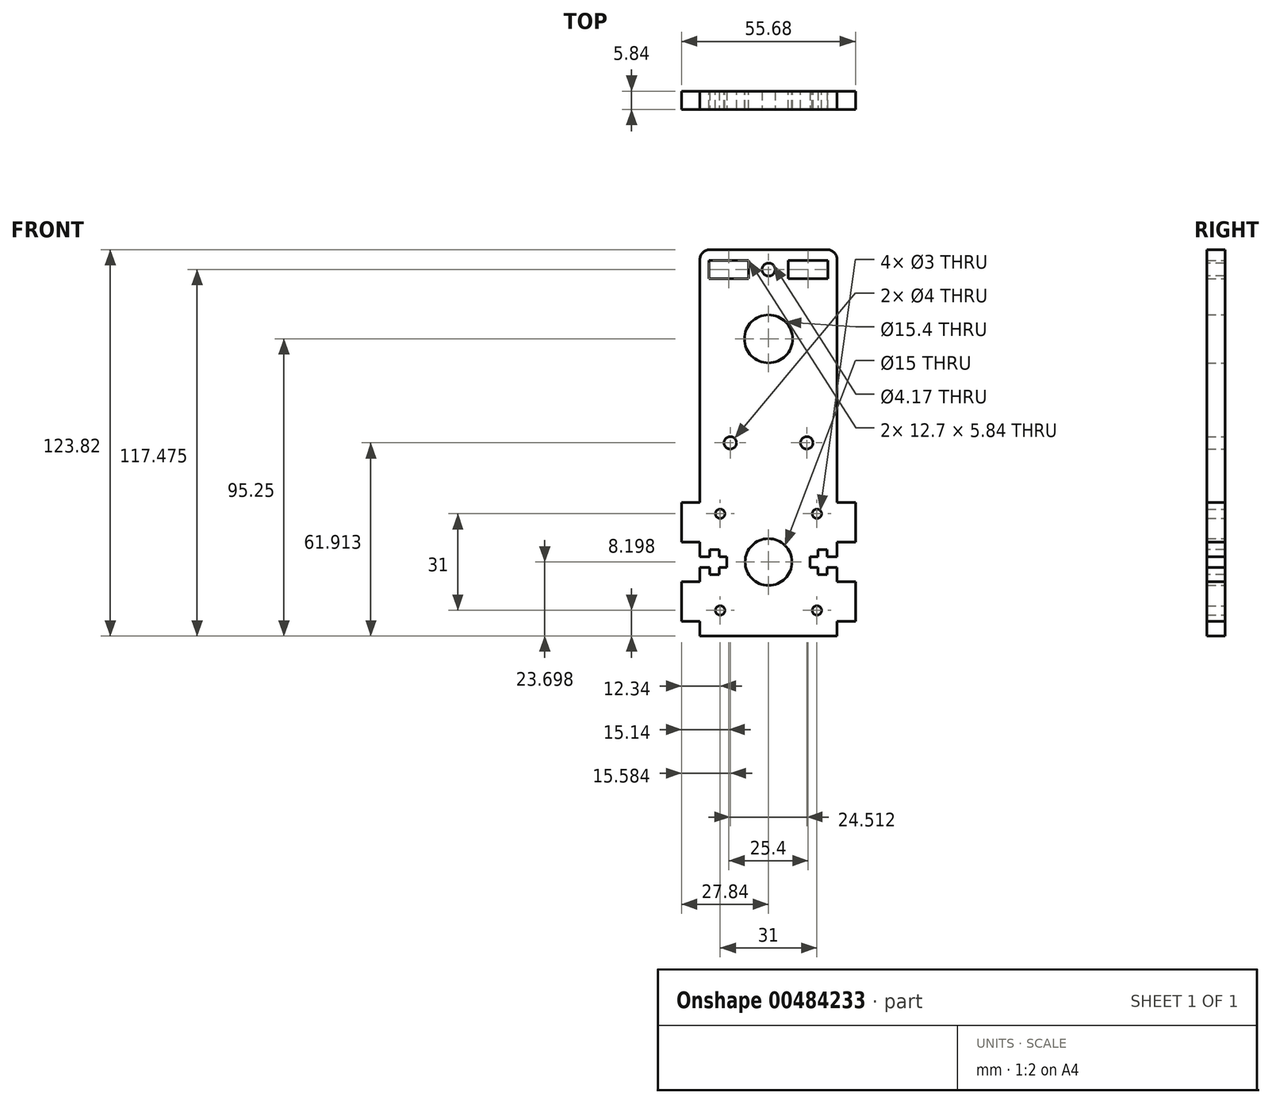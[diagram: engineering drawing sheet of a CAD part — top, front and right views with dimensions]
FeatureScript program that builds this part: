
annotation { "Feature Type Name" : "Feature", "Feature Type Description" : "" }
export const myFeature = defineFeature(function(context is Context, id is Id, definition is map)
    precondition{}
    {
        {
            var Q0;
            Q0=qCreatedBy(makeId("Front.planeOp"),FACE);
            var sketch = newSketch(context, id + "F0", { "sketchPlane" : qUnion([Q0])});
            skCircle(sketch, "E0", {"center": v(0, 0) * mm, "radius": 7.7 * mm});
            skCircle(sketch, "E1", {"center": v(0, 0) * mm, "radius": 8 * mm, "construction": true});
            skCircle(sketch, "E2", {"center": v(0, -71.55) * mm, "radius": 7.5 * mm});
            skLineSegment(sketch, "E3.bottom", {"start": v(-22, 28.58) * mm, "end": v(22, 28.58) * mm});
            skLineSegment(sketch, "E3.top", {"start": v(-22, -95.25) * mm, "end": v(22, -95.25) * mm});
            skLineSegment(sketch, "E3.right", {"start": v(22, 28.58) * mm, "end": v(22, -52.5) * mm});
            skPoint(sketch, "E3.middle", {"position": v(0, -33.34) * mm});
            skCircle(sketch, "E4", {"center": v(0, 0) * mm, "radius": 15.88 * mm, "construction": true});
            skLineSegment(sketch, "E5.bottom", {"start": v(-21.15, -50.4) * mm, "end": v(21.15, -50.4) * mm, "construction": true});
            skLineSegment(sketch, "E5.top", {"start": v(-21.15, -92.7) * mm, "end": v(21.15, -92.7) * mm, "construction": true});
            skLineSegment(sketch, "E5.left", {"start": v(-21.15, -50.4) * mm, "end": v(-21.15, -92.7) * mm, "construction": true});
            skLineSegment(sketch, "E5.right", {"start": v(21.15, -50.4) * mm, "end": v(21.15, -92.7) * mm, "construction": true});
            skLineSegment(sketch, "E6", {"start": v(-15.77, -1.86) * mm, "end": v(-7.45, -72.43) * mm, "construction": true});
            skLineSegment(sketch, "E7", {"start": v(0, 0) * mm, "end": v(0, -71.55) * mm, "construction": true});
            skLineSegment(sketch, "E8.MirrorCS", {"start": v(15.77, -1.86) * mm, "end": v(7.45, -72.43) * mm, "construction": true});
            skLineSegment(sketch, "E9", {"start": v(-21.15, -71.55) * mm, "end": v(21.15, -71.55) * mm, "construction": true});
            skLineSegment(sketch, "E10", {"start": v(0, -92.7) * mm, "end": v(0, -50.4) * mm, "construction": true});
            skCircle(sketch, "E11", {"center": v(-15.5, -56.05) * mm, "radius": 1.5 * mm});
            skCircle(sketch, "E12.MirrorC", {"center": v(15.5, -56.05) * mm, "radius": 1.5 * mm});
            skCircle(sketch, "E13.MirrorC", {"center": v(15.5, -87.05) * mm, "radius": 1.5 * mm});
            skCircle(sketch, "E14.MirrorC", {"center": v(-15.5, -87.05) * mm, "radius": 1.5 * mm});
            skLineSegment(sketch, "E15.bottom", {"start": v(-22, -77.9) * mm, "end": v(-27.84, -77.9) * mm});
            skLineSegment(sketch, "E15.top", {"start": v(-22, -90.6) * mm, "end": v(-27.84, -90.6) * mm});
            skLineSegment(sketch, "E15.right", {"start": v(-27.84, -77.9) * mm, "end": v(-27.84, -90.6) * mm});
            skPoint(sketch, "E15.middle", {"position": v(-24.92, -84.25) * mm});
            skLineSegment(sketch, "E16.MirrorCS", {"start": v(-22, -65.2) * mm, "end": v(-27.84, -65.2) * mm});
            skLineSegment(sketch, "E17.MirrorCS", {"start": v(-27.84, -65.2) * mm, "end": v(-27.84, -52.5) * mm});
            skLineSegment(sketch, "E18.MirrorCS", {"start": v(-22, -52.5) * mm, "end": v(-27.84, -52.5) * mm});
            skLineSegment(sketch, "E19.trimOffspring", {"start": v(-22, -65.2) * mm, "end": v(-22, -77.9) * mm});
            skLineSegment(sketch, "E20.trimOffspring", {"start": v(-22, -90.6) * mm, "end": v(-22, -95.25) * mm});
            skLineSegment(sketch, "E21", {"start": v(-22, -52.5) * mm, "end": v(-22, 28.58) * mm});
            skLineSegment(sketch, "E22.bottom", {"start": v(-6.35, 25.15) * mm, "end": v(-19.05, 25.15) * mm});
            skLineSegment(sketch, "E22.top", {"start": v(-6.35, 19.3) * mm, "end": v(-19.05, 19.3) * mm});
            skLineSegment(sketch, "E22.left", {"start": v(-6.35, 25.15) * mm, "end": v(-6.35, 19.3) * mm});
            skLineSegment(sketch, "E22.right", {"start": v(-19.05, 25.15) * mm, "end": v(-19.05, 19.3) * mm});
            skPoint(sketch, "E22.middle", {"position": v(-12.7, 22.23) * mm});
            skLineSegment(sketch, "E23.MirrorCS", {"start": v(6.35, 25.15) * mm, "end": v(6.35, 19.3) * mm});
            skLineSegment(sketch, "E24.MirrorCS", {"start": v(6.35, 25.15) * mm, "end": v(19.05, 25.15) * mm});
            skLineSegment(sketch, "E25.MirrorCS", {"start": v(19.05, 25.15) * mm, "end": v(19.05, 19.3) * mm});
            skLineSegment(sketch, "E26.MirrorCS", {"start": v(6.35, 19.3) * mm, "end": v(19.05, 19.3) * mm});
            skLineSegment(sketch, "E27.MirrorCS", {"start": v(22, -52.5) * mm, "end": v(27.84, -52.5) * mm});
            skLineSegment(sketch, "E28.MirrorCS", {"start": v(27.84, -65.2) * mm, "end": v(27.84, -52.5) * mm});
            skLineSegment(sketch, "E29.MirrorCS", {"start": v(22, -77.9) * mm, "end": v(27.84, -77.9) * mm});
            skLineSegment(sketch, "E30.MirrorCS", {"start": v(27.84, -77.9) * mm, "end": v(27.84, -90.6) * mm});
            skLineSegment(sketch, "E31.MirrorCS", {"start": v(22, -90.6) * mm, "end": v(27.84, -90.6) * mm});
            skLineSegment(sketch, "E32", {"start": v(27.84, -65.2) * mm, "end": v(22, -65.2) * mm});
            skLineSegment(sketch, "E33.trimOffspring", {"start": v(22, -65.2) * mm, "end": v(22, -77.9) * mm});
            skLineSegment(sketch, "E34.trimOffspring", {"start": v(22, -90.6) * mm, "end": v(22, -95.25) * mm});
            skLineSegment(sketch, "E35", {"start": v(0, -33.34) * mm, "end": v(22, -33.34) * mm, "construction": true});
            skLineSegment(sketch, "E36", {"start": v(0, -33.34) * mm, "end": v(-22, -33.34) * mm, "construction": true});
            skCircle(sketch, "E37", {"center": v(-12.26, -33.34) * mm, "radius": 2 * mm});
            skPoint(sketch, "E38", {"position": v(-12.06, -33.34) * mm});
            skCircle(sketch, "E39.MirrorC", {"center": v(12.26, -33.34) * mm, "radius": 2 * mm});
            skSolve(sketch);
        }
        {
            var Q0;
            Q0=qSketchRegion(id+"F0",true);
            extrude(context, id + "F1", {"entities" : qUnion([Q0]), "depth" : 5.84 * mm});
        }
        {
            var Q0;
            Q0=makeQuery(id+"F1.opExtrude","SWEPT_EDGE",EDGE,{"disambiguationData":[OSD([sQuery(id+"F0.wireOp",EDGE,"E3.bottom"),sQuery(id+"F0.wireOp",EDGE,"E21")])]});
            var Q1;
            Q1=makeQuery(id+"F1.opExtrude","SWEPT_EDGE",EDGE,{"disambiguationData":[OSD([sQuery(id+"F0.wireOp",EDGE,"E3.bottom"),sQuery(id+"F0.wireOp",EDGE,"E3.right")])]});
            fillet(context, id + "F2", {"entities" : qUnion([Q0, Q1]), "radius" : 3.17 * mm, "tangentPropagation" : true, "allowEdgeOverflow" : false});
        }
        {
            var Q0;
            Q0=makeQuery(id+"F1.opExtrude","CAP_FACE",FACE,{"disambiguationData":[OSD([sQuery(id+"F0.wireOp",EDGE,"E0"),sQuery(id+"F0.wireOp",EDGE,"E2"),sQuery(id+"F0.wireOp",EDGE,"E3.bottom"),sQuery(id+"F0.wireOp",EDGE,"E3.top"),sQuery(id+"F0.wireOp",EDGE,"E3.right"),sQuery(id+"F0.wireOp",EDGE,"E12.MirrorC"),sQuery(id+"F0.wireOp",EDGE,"E11"),sQuery(id+"F0.wireOp",EDGE,"E13.MirrorC"),sQuery(id+"F0.wireOp",EDGE,"E14.MirrorC"),sQuery(id+"F0.wireOp",EDGE,"E15.bottom"),sQuery(id+"F0.wireOp",EDGE,"E15.top"),sQuery(id+"F0.wireOp",EDGE,"E15.right"),sQuery(id+"F0.wireOp",EDGE,"E16.MirrorCS"),sQuery(id+"F0.wireOp",EDGE,"E17.MirrorCS"),sQuery(id+"F0.wireOp",EDGE,"E18.MirrorCS"),sQuery(id+"F0.wireOp",EDGE,"E19.trimOffspring"),sQuery(id+"F0.wireOp",EDGE,"E20.trimOffspring"),sQuery(id+"F0.wireOp",EDGE,"E21"),sQuery(id+"F0.wireOp",EDGE,"E22.bottom"),sQuery(id+"F0.wireOp",EDGE,"E22.top"),sQuery(id+"F0.wireOp",EDGE,"E22.left"),sQuery(id+"F0.wireOp",EDGE,"E22.right"),sQuery(id+"F0.wireOp",EDGE,"E23.MirrorCS"),sQuery(id+"F0.wireOp",EDGE,"E24.MirrorCS"),sQuery(id+"F0.wireOp",EDGE,"E25.MirrorCS"),sQuery(id+"F0.wireOp",EDGE,"E26.MirrorCS"),sQuery(id+"F0.wireOp",EDGE,"E27.MirrorCS"),sQuery(id+"F0.wireOp",EDGE,"E28.MirrorCS"),sQuery(id+"F0.wireOp",EDGE,"E29.MirrorCS"),sQuery(id+"F0.wireOp",EDGE,"E30.MirrorCS"),sQuery(id+"F0.wireOp",EDGE,"E31.MirrorCS"),sQuery(id+"F0.wireOp",EDGE,"E32"),sQuery(id+"F0.wireOp",EDGE,"E33.trimOffspring"),sQuery(id+"F0.wireOp",EDGE,"E34.trimOffspring"),sQuery(id+"F0.wireOp",EDGE,"E37"),sQuery(id+"F0.wireOp",EDGE,"E39.MirrorC")])],"isStart":false});
            var sketch = newSketch(context, id + "F3", { "sketchPlane" : qUnion([Q0])});
            skLineSegment(sketch, "E40", {"start": v(-22, -71.55) * mm, "end": v(22, -71.55) * mm, "construction": true});
            skLineSegment(sketch, "E41.bottom", {"start": v(-22, -69.8) * mm, "end": v(-18.83, -69.8) * mm});
            skLineSegment(sketch, "E41.top", {"start": v(-22, -73.3) * mm, "end": v(-18.83, -73.3) * mm});
            skLineSegment(sketch, "E41.left", {"start": v(-22, -69.8) * mm, "end": v(-22, -73.3) * mm});
            skPoint(sketch, "E41.middle", {"position": v(-20.41, -71.55) * mm});
            skLineSegment(sketch, "E42.bottom", {"start": v(-18.83, -67.58) * mm, "end": v(-15.85, -67.58) * mm});
            skLineSegment(sketch, "E42.top", {"start": v(-18.83, -75.52) * mm, "end": v(-15.85, -75.52) * mm});
            skLineSegment(sketch, "E42.left", {"start": v(-18.83, -67.58) * mm, "end": v(-18.83, -69.8) * mm});
            skLineSegment(sketch, "E42.right", {"start": v(-15.85, -67.58) * mm, "end": v(-15.85, -69.8) * mm});
            skPoint(sketch, "E42.middle", {"position": v(-17.34, -71.55) * mm});
            skLineSegment(sketch, "E43.trimOffspring", {"start": v(-18.83, -73.3) * mm, "end": v(-18.83, -75.52) * mm});
            skLineSegment(sketch, "E44.bottom", {"start": v(-15.85, -69.8) * mm, "end": v(-13.35, -69.8) * mm});
            skLineSegment(sketch, "E44.top", {"start": v(-15.85, -73.3) * mm, "end": v(-13.35, -73.3) * mm});
            skLineSegment(sketch, "E44.right", {"start": v(-13.35, -69.8) * mm, "end": v(-13.35, -73.3) * mm});
            skPoint(sketch, "E44.middle", {"position": v(-14.6, -71.55) * mm});
            skLineSegment(sketch, "E45.trimOffspring", {"start": v(-15.85, -73.3) * mm, "end": v(-15.85, -75.52) * mm});
            skLineSegment(sketch, "E46", {"start": v(0, -54.52) * mm, "end": v(0, -71.55) * mm, "construction": true});
            skLineSegment(sketch, "E47.MirrorCS", {"start": v(22, -69.8) * mm, "end": v(18.82, -69.8) * mm});
            skLineSegment(sketch, "E48.MirrorCS", {"start": v(22, -73.3) * mm, "end": v(18.82, -73.3) * mm});
            skPoint(sketch, "E49.MirrorP", {"position": v(14.6, -71.55) * mm});
            skLineSegment(sketch, "E50.MirrorCS", {"start": v(22, -69.8) * mm, "end": v(22, -73.3) * mm});
            skLineSegment(sketch, "E51.MirrorCS", {"start": v(18.82, -67.58) * mm, "end": v(15.85, -67.58) * mm});
            skLineSegment(sketch, "E52.MirrorCS", {"start": v(18.82, -75.52) * mm, "end": v(15.85, -75.52) * mm});
            skLineSegment(sketch, "E53.MirrorCS", {"start": v(15.85, -67.58) * mm, "end": v(15.85, -69.8) * mm});
            skLineSegment(sketch, "E54.MirrorCS", {"start": v(18.82, -73.3) * mm, "end": v(18.82, -75.52) * mm});
            skLineSegment(sketch, "E55.MirrorCS", {"start": v(15.85, -69.8) * mm, "end": v(13.35, -69.8) * mm});
            skLineSegment(sketch, "E56.MirrorCS", {"start": v(22, -71.55) * mm, "end": v(-22, -71.55) * mm, "construction": true});
            skPoint(sketch, "E57.MirrorP", {"position": v(17.34, -71.55) * mm});
            skLineSegment(sketch, "E58.MirrorCS", {"start": v(18.82, -67.58) * mm, "end": v(18.82, -69.8) * mm});
            skPoint(sketch, "E59.MirrorP", {"position": v(20.41, -71.55) * mm});
            skLineSegment(sketch, "E60.MirrorCS", {"start": v(15.85, -73.3) * mm, "end": v(13.35, -73.3) * mm});
            skLineSegment(sketch, "E61.MirrorCS", {"start": v(15.85, -73.3) * mm, "end": v(15.85, -75.52) * mm});
            skLineSegment(sketch, "E62.MirrorCS", {"start": v(13.35, -69.8) * mm, "end": v(13.35, -73.3) * mm});
            skSolve(sketch);
        }
        {
            var Q0;
            Q0=qSketchRegion(id+"F3",true);
            extrude(context, id + "F4", {"entities" : qUnion([Q0]), "operationType" : NewBodyOperationType.REMOVE, "endBound" : BoundingType.THROUGH_ALL, "oppositeDirection" : true, "depth" : 25.4 * mm});
        }
        {
            var Q0;
            Q0=makeQuery(id+"F1.opExtrude","CAP_FACE",FACE,{"disambiguationData":[OSD([sQuery(id+"F0.wireOp",EDGE,"E0"),sQuery(id+"F0.wireOp",EDGE,"E2"),sQuery(id+"F0.wireOp",EDGE,"E3.bottom"),sQuery(id+"F0.wireOp",EDGE,"E3.top"),sQuery(id+"F0.wireOp",EDGE,"E3.right"),sQuery(id+"F0.wireOp",EDGE,"E12.MirrorC"),sQuery(id+"F0.wireOp",EDGE,"E11"),sQuery(id+"F0.wireOp",EDGE,"E13.MirrorC"),sQuery(id+"F0.wireOp",EDGE,"E14.MirrorC"),sQuery(id+"F0.wireOp",EDGE,"E15.bottom"),sQuery(id+"F0.wireOp",EDGE,"E15.top"),sQuery(id+"F0.wireOp",EDGE,"E15.right"),sQuery(id+"F0.wireOp",EDGE,"E16.MirrorCS"),sQuery(id+"F0.wireOp",EDGE,"E17.MirrorCS"),sQuery(id+"F0.wireOp",EDGE,"E18.MirrorCS"),sQuery(id+"F0.wireOp",EDGE,"E19.trimOffspring"),sQuery(id+"F0.wireOp",EDGE,"E20.trimOffspring"),sQuery(id+"F0.wireOp",EDGE,"E21"),sQuery(id+"F0.wireOp",EDGE,"E22.bottom"),sQuery(id+"F0.wireOp",EDGE,"E22.top"),sQuery(id+"F0.wireOp",EDGE,"E22.left"),sQuery(id+"F0.wireOp",EDGE,"E22.right"),sQuery(id+"F0.wireOp",EDGE,"E23.MirrorCS"),sQuery(id+"F0.wireOp",EDGE,"E24.MirrorCS"),sQuery(id+"F0.wireOp",EDGE,"E25.MirrorCS"),sQuery(id+"F0.wireOp",EDGE,"E26.MirrorCS"),sQuery(id+"F0.wireOp",EDGE,"E27.MirrorCS"),sQuery(id+"F0.wireOp",EDGE,"E28.MirrorCS"),sQuery(id+"F0.wireOp",EDGE,"E29.MirrorCS"),sQuery(id+"F0.wireOp",EDGE,"E30.MirrorCS"),sQuery(id+"F0.wireOp",EDGE,"E31.MirrorCS"),sQuery(id+"F0.wireOp",EDGE,"E32"),sQuery(id+"F0.wireOp",EDGE,"E33.trimOffspring"),sQuery(id+"F0.wireOp",EDGE,"E34.trimOffspring"),sQuery(id+"F0.wireOp",EDGE,"E37"),sQuery(id+"F0.wireOp",EDGE,"E39.MirrorC")])],"isStart":false});
            var sketch = newSketch(context, id + "F5", { "sketchPlane" : qUnion([Q0])});
            skLineSegment(sketch, "E63", {"start": v(-6.35, 22.23) * mm, "end": v(6.35, 22.23) * mm, "construction": true});
            skCircle(sketch, "E64", {"center": v(0, 22.23) * mm, "radius": 2.08 * mm});
            skSolve(sketch);
        }
        {
            var Q0;
            Q0=qSketchRegion(id+"F5",true);
            extrude(context, id + "F6", {"entities" : qUnion([Q0]), "operationType" : NewBodyOperationType.REMOVE, "oppositeDirection" : true, "depth" : 25.4 * mm});
        }
    });
